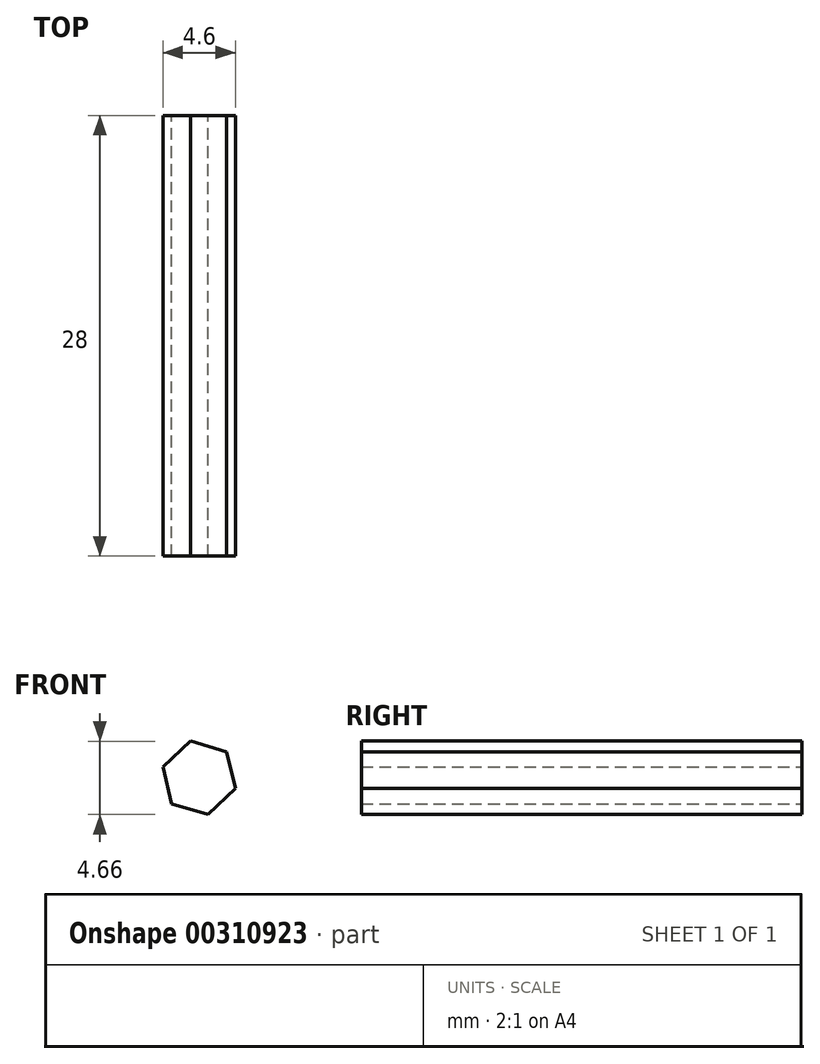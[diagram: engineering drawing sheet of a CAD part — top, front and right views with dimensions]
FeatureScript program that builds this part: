
annotation { "Feature Type Name" : "Feature", "Feature Type Description" : "" }
export const myFeature = defineFeature(function(context is Context, id is Id, definition is map)
    precondition{}
    {
        {
            var Q0;
            Q0=qCreatedBy(makeId("Front.planeOp"),FACE);
            var sketch = newSketch(context, id + "F0", { "sketchPlane" : qUnion([Q0])});
            skCircle(sketch, "E0.cCircle", {"center": v(0, 0) * mm, "radius": 2.08 * mm, "construction": true});
            skLineSegment(sketch, "E0.0", {"start": v(-2.3, 0.68) * mm, "end": v(-0.56, 2.33) * mm});
            skLineSegment(sketch, "E0.1", {"start": v(-0.56, 2.33) * mm, "end": v(1.74, 1.65) * mm});
            skLineSegment(sketch, "E0.2", {"start": v(1.74, 1.65) * mm, "end": v(2.3, -0.68) * mm});
            skLineSegment(sketch, "E0.3", {"start": v(2.3, -0.68) * mm, "end": v(0.56, -2.33) * mm});
            skLineSegment(sketch, "E0.4", {"start": v(0.56, -2.33) * mm, "end": v(-1.74, -1.65) * mm});
            skLineSegment(sketch, "E0.5", {"start": v(-1.74, -1.65) * mm, "end": v(-2.3, 0.68) * mm});
            skPoint(sketch, "E0.0.midPoint", {"position": v(-1.43, 1.5) * mm});
            skSolve(sketch);
        }
        {
            var Q0;
            Q0=makeQuery(id+"F0.imprint","IMPRINT",FACE,{"disambiguationData":[TD([[makeQuery(id+"F0.imprint","IMPRINT",EDGE,{"derivedFrom":sQuery(id+"F0.wireOp",EDGE,"E0.0")}),-1.0]])]});
            extrude(context, id + "F1", {"entities" : qUnion([Q0]), "depth" : 28 * mm});
        }
    });
